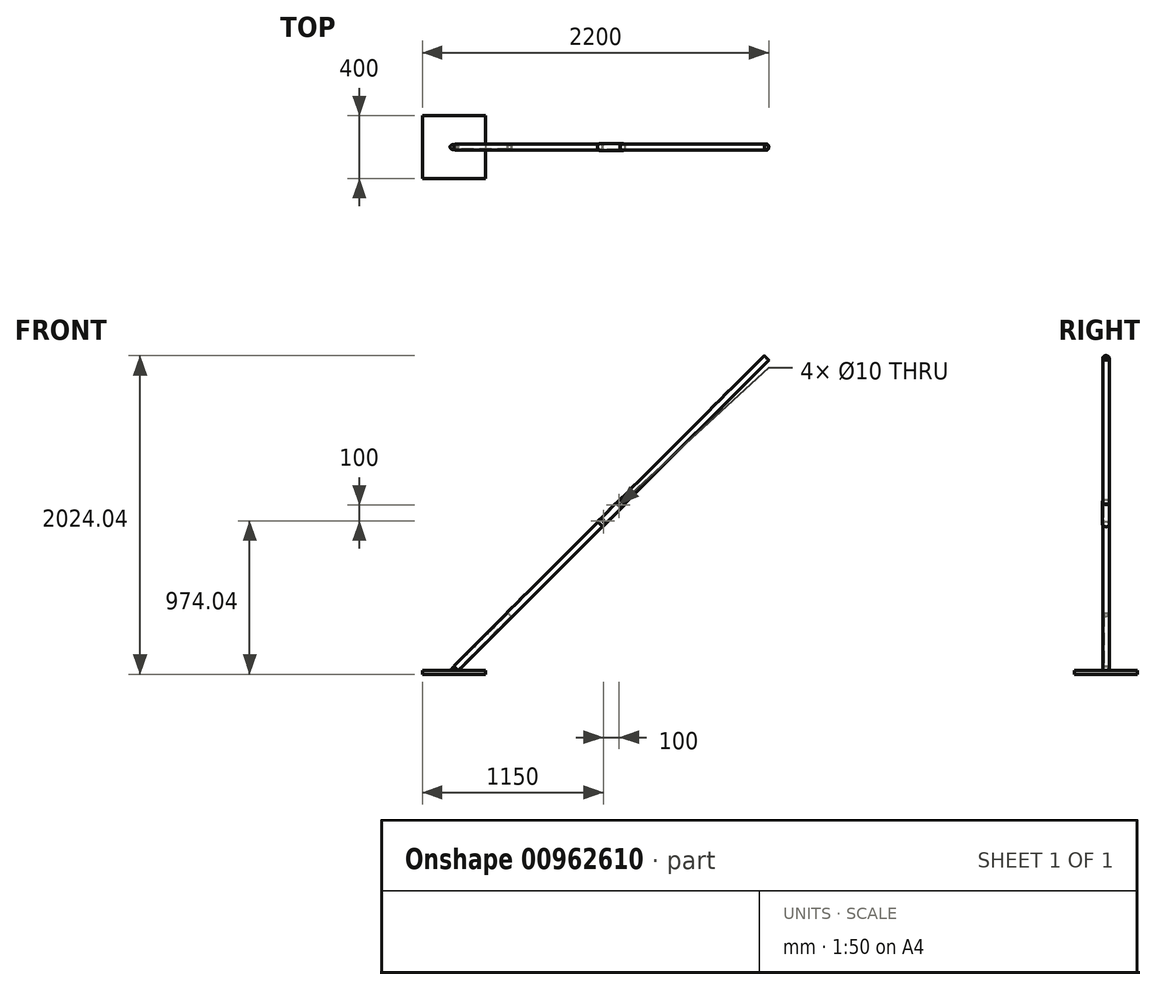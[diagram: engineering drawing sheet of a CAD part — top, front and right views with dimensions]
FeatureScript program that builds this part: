
annotation { "Feature Type Name" : "Feature", "Feature Type Description" : "" }
export const myFeature = defineFeature(function(context is Context, id is Id, definition is map)
    precondition{}
    {
        {
            var Q0;
            Q0=qCreatedBy(makeId("Top.planeOp"),FACE);
            var sketch = newSketch(context, id + "F0", { "sketchPlane" : qUnion([Q0])});
            skLineSegment(sketch, "E0.bottom", {"start": v(-200, 200) * mm, "end": v(200, 200) * mm});
            skLineSegment(sketch, "E0.top", {"start": v(-200, -200) * mm, "end": v(200, -200) * mm});
            skLineSegment(sketch, "E0.left", {"start": v(-200, 200) * mm, "end": v(-200, -200) * mm});
            skLineSegment(sketch, "E0.right", {"start": v(200, 200) * mm, "end": v(200, -200) * mm});
            skLineSegment(sketch, "E1", {"start": v(200, 0) * mm, "end": v(-200, 0) * mm, "construction": true});
            skLineSegment(sketch, "E2", {"start": v(0, 200) * mm, "end": v(0, -200) * mm, "construction": true});
            skLineSegment(sketch, "E3", {"start": v(200, 46) * mm, "end": v(-200, 46) * mm, "construction": true});
            skSolve(sketch);
        }
        {
            var Q0;
            Q0=makeQuery(id+"F0.imprint","IMPRINT",FACE,{"disambiguationData":[TD([[makeQuery(id+"F0.imprint","IMPRINT",EDGE,{"derivedFrom":sQuery(id+"F0.wireOp",EDGE,"E0.bottom")}),-1.0]])]});
            extrude(context, id + "F1", {"entities" : qUnion([Q0]), "oppositeDirection" : true, "depth" : 24 * mm, "offsetDistance" : 25 * mm});
        }
        {
            var Q0;
            Q0=qCreatedBy(makeId("Front.planeOp"),FACE);
            cPlane(context, id + "F2", {"entities" : qUnion([Q0]), "cplaneType" : CPlaneType.OFFSET, "offset" : 0 * mm, "oppositeDirection" : true, "width" : 150 * mm, "height" : 150 * mm});
        }
        {
            var Q0;
            Q0=qCreatedBy(id+"F2.planeOp",FACE);
            var sketch = newSketch(context, id + "F3", { "sketchPlane" : qUnion([Q0])});
            skLineSegment(sketch, "E4", {"start": v(0, 0) * mm, "end": v(353.55, 353.55) * mm, "construction": true});
            skLineSegment(sketch, "E5", {"start": v(353.55, 353.55) * mm, "end": v(365.57, 341.53) * mm, "construction": true});
            skLineSegment(sketch, "E6", {"start": v(353.55, 353.55) * mm, "end": v(341.53, 365.57) * mm, "construction": true});
            skLineSegment(sketch, "E7", {"start": v(341.53, 365.57) * mm, "end": v(-24.04, 0) * mm});
            skLineSegment(sketch, "E8", {"start": v(341.53, 365.57) * mm, "end": v(343.65, 363.45) * mm});
            skLineSegment(sketch, "E9", {"start": v(343.65, 363.45) * mm, "end": v(-19.8, 0) * mm});
            skLineSegment(sketch, "E10", {"start": v(-19.8, 0) * mm, "end": v(-24.04, 0) * mm});
            skSolve(sketch);
        }
        {
            var Q0;
            Q0 = qSketchRegion(id + "F3", true);
            var Q1;
            Q1=sQuery(id+"F3.wireOp",EDGE,"E4");
            revolve(context, id + "F4", {"operationType" : NewBodyOperationType.ADD, "surfaceOperationType" : NewSurfaceOperationType.NEW, "entities" : qUnion([Q0]), "axis" : qUnion([Q1]), "revolveType" : RevolveType.FULL});
        }
        {
            var Q0;
            Q0=qCreatedBy(id+"F2.planeOp",FACE);
            var sketch = newSketch(context, id + "F5", { "sketchPlane" : qUnion([Q0])});
            skLineSegment(sketch, "E11", {"start": v(0, 0) * mm, "end": v(0, 2000) * mm, "construction": true});
            skLineSegment(sketch, "E12", {"start": v(0, 0) * mm, "end": v(2000, 0) * mm, "construction": true});
            skLineSegment(sketch, "E13", {"start": v(2000, 2000) * mm, "end": v(0, 2000) * mm, "construction": true});
            skLineSegment(sketch, "E14", {"start": v(2000, 2000) * mm, "end": v(2000, 0) * mm, "construction": true});
            skLineSegment(sketch, "E15", {"start": v(0, 0) * mm, "end": v(2000, 2000) * mm, "construction": true});
            skLineSegment(sketch, "E16", {"start": v(1971.72, 2000) * mm, "end": v(2000, 1971.72) * mm, "construction": true});
            skLineSegment(sketch, "E17", {"start": v(1971.72, 2000) * mm, "end": v(1973.84, 1997.88) * mm});
            skLineSegment(sketch, "E18", {"start": v(1971.72, 2000) * mm, "end": v(0, 28.28) * mm});
            skLineSegment(sketch, "E19", {"start": v(1973.84, 1997.88) * mm, "end": v(2.12, 26.16) * mm});
            skLineSegment(sketch, "E20", {"start": v(0, 28.28) * mm, "end": v(2.12, 26.16) * mm});
            skLineSegment(sketch, "E21", {"start": v(1000, 0) * mm, "end": v(1000, 1000) * mm, "construction": true});
            skSolve(sketch);
        }
        {
            var Q0;
            Q0 = qSketchRegion(id + "F5", true);
            var Q1;
            Q1=sQuery(id+"F5.wireOp",EDGE,"E15");
            revolve(context, id + "F6", {"surfaceOperationType" : NewSurfaceOperationType.NEW, "entities" : qUnion([Q0]), "axis" : qUnion([Q1]), "revolveType" : RevolveType.FULL});
        }
        {
            var Q0;
            Q0=qCreatedBy(id+"F2.planeOp",FACE);
            var sketch = newSketch(context, id + "F7", { "sketchPlane" : qUnion([Q0])});
            skLineSegment(sketch, "E22", {"start": v(0, 0) * mm, "end": v(1000, 0) * mm, "construction": true});
            skLineSegment(sketch, "E23", {"start": v(1000, 0) * mm, "end": v(1000, 1000) * mm, "construction": true});
            skLineSegment(sketch, "E24", {"start": v(1000, 1000) * mm, "end": v(1070.71, 1070.71) * mm, "construction": true});
            skLineSegment(sketch, "E25", {"start": v(1056.57, 1084.85) * mm, "end": v(1054.45, 1086.97) * mm});
            skLineSegment(sketch, "E26", {"start": v(1056.57, 1084.85) * mm, "end": v(985.86, 1014.14) * mm});
            skLineSegment(sketch, "E27", {"start": v(1054.45, 1086.97) * mm, "end": v(983.74, 1016.26) * mm});
            skLineSegment(sketch, "E28", {"start": v(983.74, 1016.26) * mm, "end": v(985.86, 1014.14) * mm});
            skLineSegment(sketch, "E29", {"start": v(1070.71, 1070.71) * mm, "end": v(1054.45, 1086.97) * mm, "construction": true});
            skPoint(sketch, "E30", {"position": v(1000, 1000) * mm});
            skSolve(sketch);
        }
        {
            var Q0;
            Q0 = qSketchRegion(id + "F7", true);
            var Q1;
            Q1=sQuery(id+"F7.wireOp",EDGE,"E24");
            revolve(context, id + "F8", {"surfaceOperationType" : NewSurfaceOperationType.NEW, "entities" : qUnion([Q0]), "axis" : qUnion([Q1]), "revolveType" : RevolveType.FULL});
        }
        {
            var Q0;
            Q0=makeQuery(id+"F8.opRevolve","SWEPT_BODY",BODY,{"disambiguationData":[OSD([sQuery(id+"F7.wireOp",EDGE,"E25"),sQuery(id+"F7.wireOp",EDGE,"E26"),sQuery(id+"F7.wireOp",EDGE,"E27"),sQuery(id+"F7.wireOp",EDGE,"E28")])]});
            var Q1;
            Q1=makeQuery(id+"F8.opRevolve","SWEPT_FACE",FACE,{"disambiguationData":[OSD([sQuery(id+"F7.wireOp",EDGE,"E28")])]});
            mirror(context, id + "F9", {"operationType" : NewBodyOperationType.ADD, "entities" : qUnion([Q0]), "mirrorPlane" : qUnion([Q1])});
        }
        {
            var Q0;
            Q0=qCreatedBy(id+"F2.planeOp",FACE);
            var sketch = newSketch(context, id + "F10", { "sketchPlane" : qUnion([Q0])});
            skLineSegment(sketch, "E31.bottom", {"start": v(1050, 950) * mm, "end": v(950, 950) * mm, "construction": true});
            skLineSegment(sketch, "E31.top", {"start": v(1050, 1050) * mm, "end": v(950, 1050) * mm, "construction": true});
            skLineSegment(sketch, "E31.left", {"start": v(1050, 950) * mm, "end": v(1050, 1050) * mm, "construction": true});
            skLineSegment(sketch, "E31.right", {"start": v(950, 950) * mm, "end": v(950, 1050) * mm, "construction": true});
            skPoint(sketch, "E31.middle", {"position": v(1000, 1000) * mm});
            skCircle(sketch, "E32", {"center": v(950, 950) * mm, "radius": 5 * mm});
            skCircle(sketch, "E33", {"center": v(1050, 1050) * mm, "radius": 5 * mm});
            skSolve(sketch);
        }
        {
            var Q0;
            Q0 = qSketchRegion(id + "F10", true);
            extrude(context, id + "F11", {"entities" : qUnion([Q0]), "operationType" : NewBodyOperationType.REMOVE, "endBound" : BoundingType.THROUGH_ALL, "oppositeDirection" : true, "depth" : 25 * mm, "offsetDistance" : 25 * mm, "hasSecondDirection" : true, "secondDirectionBound" : SecondDirectionBoundingType.THROUGH_ALL, "secondDirectionOppositeDirection" : false, "secondDirectionDepth" : 25 * mm});
        }
    });
